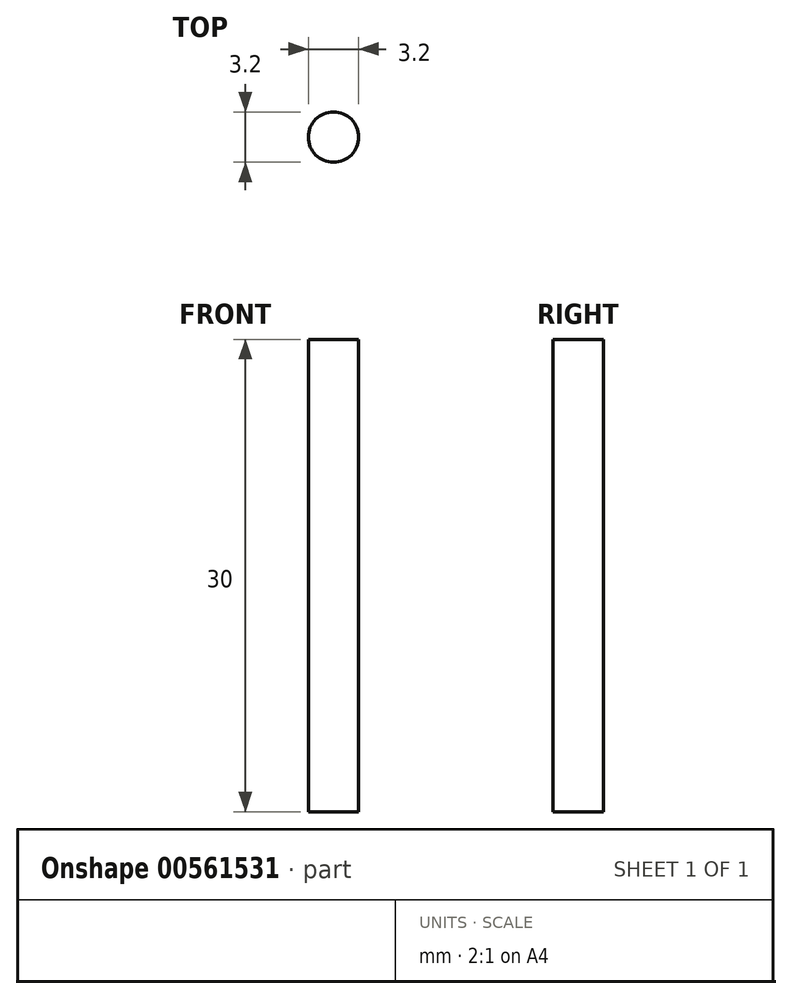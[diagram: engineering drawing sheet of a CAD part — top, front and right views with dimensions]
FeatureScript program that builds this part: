
annotation { "Feature Type Name" : "Feature", "Feature Type Description" : "" }
export const myFeature = defineFeature(function(context is Context, id is Id, definition is map)
    precondition{}
    {
        {
            var Q0;
            Q0=qCreatedBy(makeId("Top.planeOp"),FACE);
            var sketch = newSketch(context, id + "F0", { "sketchPlane" : qUnion([Q0])});
            skCircle(sketch, "E0", {"center": v(0, 0) * mm, "radius": 1.6 * mm});
            skSolve(sketch);
        }
        {
            var Q0;
            Q0 = qSketchRegion(id + "F0", true);
            extrude(context, id + "F1", {"entities" : qUnion([Q0]), "depth" : 30 * mm, "offsetDistance" : 25 * mm, "symmetric" : true});
        }
    });
